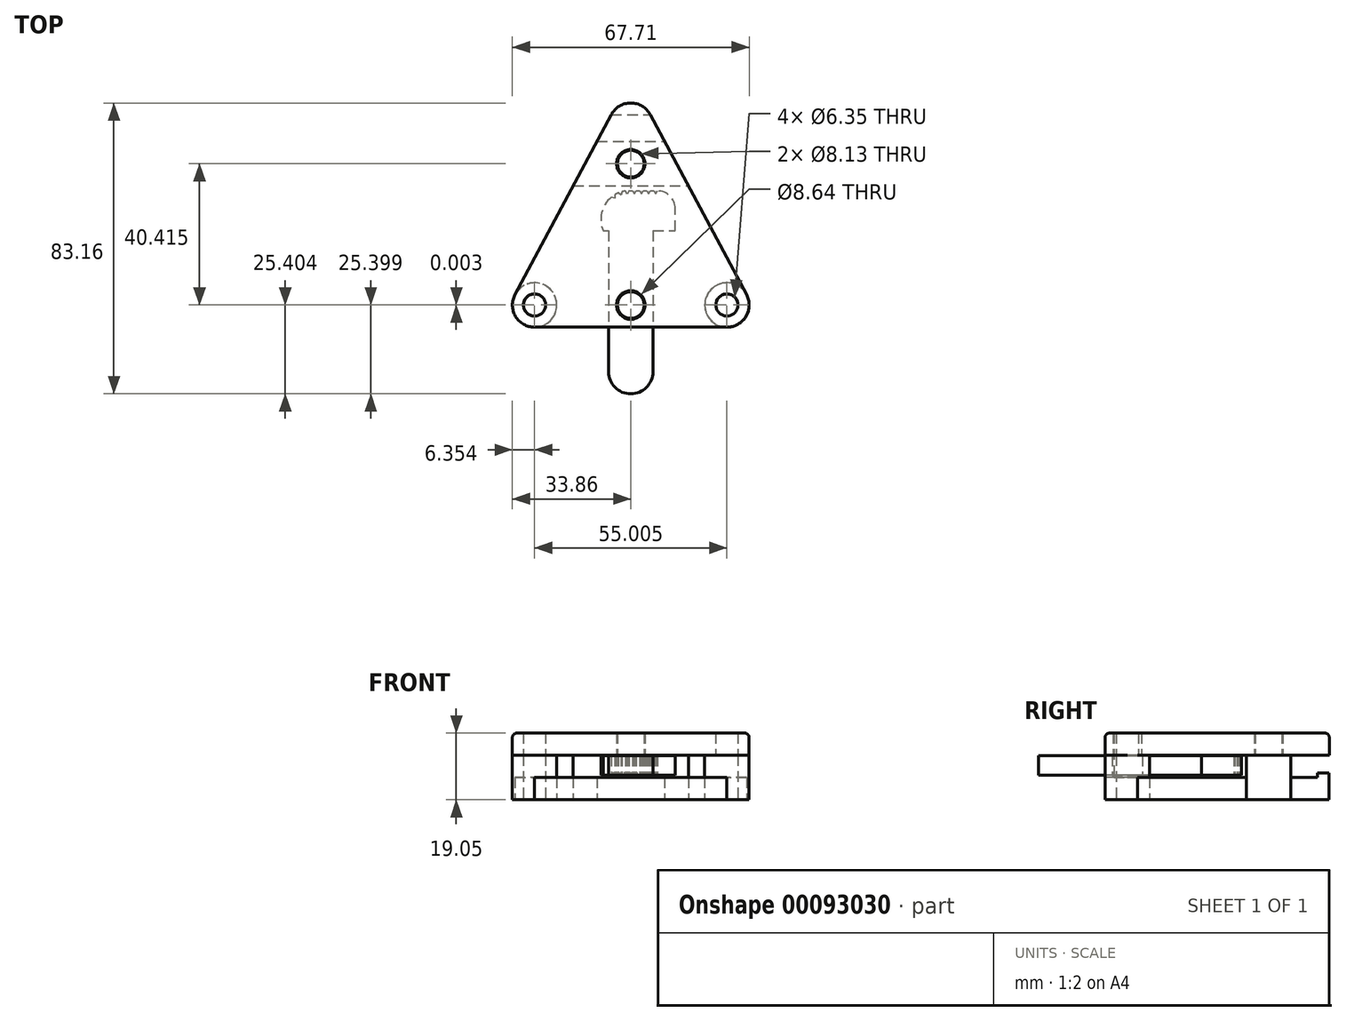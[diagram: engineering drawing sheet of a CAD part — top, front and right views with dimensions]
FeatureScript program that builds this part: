
annotation { "Feature Type Name" : "Feature", "Feature Type Description" : "" }
export const myFeature = defineFeature(function(context is Context, id is Id, definition is map)
    precondition{}
    {
        {
            var Q0;
            Q0=qCreatedBy(makeId("Top.planeOp"),FACE);
            var sketch = newSketch(context, id + "F0", { "sketchPlane" : qUnion([Q0])});
            skPoint(sketch, "E0.middle", {"position": v(0, 0) * mm});
            skLineSegment(sketch, "E1", {"start": v(27.5, -35.6) * mm, "end": v(-27.5, -35.6) * mm});
            skLineSegment(sketch, "E2", {"start": v(-33.1, -26.24) * mm, "end": v(-5.6, 25.13) * mm});
            skLineSegment(sketch, "E3", {"start": v(5.6, 25.13) * mm, "end": v(33.1, -26.24) * mm});
            skPoint(sketch, "E4.visualSharp", {"position": v(0, 35.6) * mm});
            skArc(sketch, "E4.filletArc", {"start": v(5.6, 25.13) * mm, "mid": v(0, 28.49) * mm, "end": v(-5.6, 25.13) * mm});
            skPoint(sketch, "E5.visualSharp", {"position": v(38.1, -35.6) * mm});
            skArc(sketch, "E5.filletArc", {"start": v(27.5, -35.6) * mm, "mid": v(32.95, -32.5) * mm, "end": v(33.1, -26.24) * mm});
            skPoint(sketch, "E6.visualSharp", {"position": v(-38.1, -35.6) * mm});
            skArc(sketch, "E6.filletArc", {"start": v(-33.1, -26.24) * mm, "mid": v(-32.95, -32.5) * mm, "end": v(-27.5, -35.6) * mm});
            skCircle(sketch, "E7", {"center": v(-27.5, -29.24) * mm, "radius": 3.18 * mm});
            skCircle(sketch, "E8", {"center": v(27.5, -29.24) * mm, "radius": 3.18 * mm});
            skPoint(sketch, "E9", {"position": v(0, -29.24) * mm});
            skCircle(sketch, "E10", {"center": v(0, -29.24) * mm, "radius": 3.81 * mm});
            skLineSegment(sketch, "E11", {"start": v(-5.6, 25.13) * mm, "end": v(5.6, 25.13) * mm});
            skLineSegment(sketch, "E12", {"start": v(-9.68, 17.51) * mm, "end": v(9.68, 17.51) * mm});
            skLineSegment(sketch, "E13", {"start": v(-16.47, 4.81) * mm, "end": v(16.47, 4.81) * mm});
            skCircle(sketch, "E14", {"center": v(-27.5, -29.24) * mm, "radius": 6.35 * mm});
            skCircle(sketch, "E15", {"center": v(27.5, -29.24) * mm, "radius": 6.35 * mm});
            skPoint(sketch, "E16", {"position": v(0, 11.16) * mm});
            skCircle(sketch, "E17", {"center": v(0, 11.16) * mm, "radius": 3.81 * mm});
            skSolve(sketch);
        }
        {
            var Q0;
            Q0=makeQuery(id+"F0.imprint","IMPRINT",FACE,{"disambiguationData":[TD([[makeQuery(id+"F0.imprint","IMPRINT",EDGE,{"derivedFrom":sQuery(id+"F0.wireOp",EDGE,"E1")}),-1.0]])]});
            var Q1;
            {var subQ0=sQuery(id+"F0.wireOp",EDGE,"E11");Q1=makeQuery(id+"F0.imprint","IMPRINT",FACE,{"disambiguationData":[TD([[makeQuery(id+"F0.imprint","IMPRINT",EDGE,{"derivedFrom":subQ0}),-1.0]])]});}
            extrude(context, id + "F1", {"entities" : qUnion([Q0, Q1]), "depth" : 6.35 * mm});
        }
        {
            var Q0;
            {var subQ0=sQuery(id+"F0.wireOp",EDGE,"E12");Q0=makeQuery(id+"F0.imprint","IMPRINT",FACE,{"disambiguationData":[TD([[makeQuery(id+"F0.imprint","IMPRINT",EDGE,{"derivedFrom":subQ0}),-1.0]])]});}
            var Q1;
            Q1=makeQuery(id+"F0.imprint","IMPRINT",FACE,{"disambiguationData":[TD([[makeQuery(id+"F0.imprint","IMPRINT",EDGE,{"derivedFrom":sQuery(id+"F0.wireOp",EDGE,"E7")}),-1.0]])]});
            var Q2;
            Q2=makeQuery(id+"F0.imprint","IMPRINT",FACE,{"disambiguationData":[TD([[makeQuery(id+"F0.imprint","IMPRINT",EDGE,{"derivedFrom":sQuery(id+"F0.wireOp",EDGE,"E8")}),-1.0]])]});
            extrude(context, id + "F2", {"entities" : qUnion([Q0, Q1, Q2]), "depth" : 12.7 * mm});
        }
        {
            var Q0;
            Q0=makeQuery(id+"F0.imprint","IMPRINT",FACE,{"disambiguationData":[TD([[makeQuery(id+"F0.imprint","IMPRINT",EDGE,{"derivedFrom":sQuery(id+"F0.wireOp",EDGE,"E10")}),1.0]])]});
            var Q1;
            Q1=makeQuery(id+"F0.imprint","IMPRINT",FACE,{"disambiguationData":[TD([[makeQuery(id+"F0.imprint","IMPRINT",EDGE,{"derivedFrom":sQuery(id+"F0.wireOp",EDGE,"E17")}),1.0]])]});
            extrude(context, id + "F3", {"entities" : qUnion([Q0, Q1]), "operationType" : NewBodyOperationType.ADD, "depth" : 19.05 * mm});
        }
        {
            var Q0;
            Q0=makeQuery(id+"F0.imprint","IMPRINT",FACE,{"disambiguationData":[TD([[makeQuery(id+"F0.imprint","IMPRINT",EDGE,{"derivedFrom":sQuery(id+"F0.wireOp",EDGE,"E4.filletArc")}),1.0]])]});
            extrude(context, id + "F4", {"entities" : qUnion([Q0]), "operationType" : NewBodyOperationType.ADD, "depth" : 7.62 * mm});
        }
        {
            var Q0;
            Q0=makeQuery(id+"F1.opExtrude","CAP_FACE",FACE,{"disambiguationData":[OSD([sQuery(id+"F0.wireOp",EDGE,"E1"),sQuery(id+"F0.wireOp",EDGE,"E2"),sQuery(id+"F0.wireOp",EDGE,"E3"),sQuery(id+"F0.wireOp",EDGE,"E10"),sQuery(id+"F0.wireOp",EDGE,"E13"),sQuery(id+"F0.wireOp",EDGE,"E14"),sQuery(id+"F0.wireOp",EDGE,"E15")])],"isStart":false});
            cPlane(context, id + "F5", {"entities" : qUnion([Q0]), "cplaneType" : CPlaneType.OFFSET, "offset" : 0 * mm, "width" : 152.4 * mm, "height" : 152.4 * mm});
        }
        {
            var Q0;
            Q0=qCreatedBy(id+"F5.planeOp",FACE);
            var sketch = newSketch(context, id + "F6", { "sketchPlane" : qUnion([Q0])});
            skLineSegment(sketch, "E18", {"start": v(-27.5, -35.59) * mm, "end": v(27.5, -35.59) * mm});
            skLineSegment(sketch, "E19", {"start": v(33.1, -26.24) * mm, "end": v(5.6, 25.17) * mm});
            skLineSegment(sketch, "E20", {"start": v(-5.6, 25.17) * mm, "end": v(-33.1, -26.24) * mm});
            skPoint(sketch, "E21.visualSharp", {"position": v(0, 35.64) * mm});
            skArc(sketch, "E21.filletArc", {"start": v(5.6, 25.17) * mm, "mid": v(0, 28.52) * mm, "end": v(-5.6, 25.17) * mm});
            skPoint(sketch, "E22.visualSharp", {"position": v(38.1, -35.59) * mm});
            skArc(sketch, "E22.filletArc", {"start": v(27.5, -35.59) * mm, "mid": v(32.95, -32.5) * mm, "end": v(33.1, -26.24) * mm});
            skPoint(sketch, "E23.visualSharp", {"position": v(-38.1, -35.59) * mm});
            skArc(sketch, "E23.filletArc", {"start": v(-33.1, -26.24) * mm, "mid": v(-32.95, -32.5) * mm, "end": v(-27.5, -35.59) * mm});
            skCircle(sketch, "E24", {"center": v(27.5, -29.24) * mm, "radius": 3.18 * mm});
            skCircle(sketch, "E25", {"center": v(-27.5, -29.24) * mm, "radius": 3.18 * mm});
            skCircle(sketch, "E26", {"center": v(0, -29.24) * mm, "radius": 4.06 * mm});
            skCircle(sketch, "E27", {"center": v(0, 11.18) * mm, "radius": 4.06 * mm});
            skSolve(sketch);
        }
        {
            var Q0;
            Q0=makeQuery(id+"F6.imprint","IMPRINT",FACE,{"disambiguationData":[TD([[makeQuery(id+"F6.imprint","IMPRINT",EDGE,{"derivedFrom":sQuery(id+"F6.wireOp",EDGE,"E18")}),1.0]])]});
            extrude(context, id + "F7", {"entities" : qUnion([Q0]), "depth" : 12.7 * mm, "hasSecondDirection" : true, "secondDirectionOppositeDirection" : false, "secondDirectionDepth" : 6.35 * mm});
        }
        {
            var Q0;
            Q0=makeQuery(id+"F7.opExtrude","CAP_EDGE",EDGE,{"disambiguationData":[OSD([sQuery(id+"F6.wireOp",EDGE,"E18")])],"isStart":false});
            fillet(context, id + "F8", {"entities" : qUnion([Q0]), "radius" : 1.27 * mm, "tangentPropagation" : true, "allowEdgeOverflow" : false});
        }
        {
            var Q0;
            Q0=qCreatedBy(id+"F5.planeOp",FACE);
            var sketch = newSketch(context, id + "F9", { "sketchPlane" : qUnion([Q0])});
            skLineSegment(sketch, "E28", {"start": v(-7.88, -8.03) * mm, "end": v(7.14, -8.03) * mm});
            skLineSegment(sketch, "E29.top", {"start": v(0, -54.64) * mm, "end": v(0, -54.64) * mm});
            skLineSegment(sketch, "E29.left", {"start": v(-6.35, -8.03) * mm, "end": v(-6.35, -48.3) * mm});
            skLineSegment(sketch, "E29.right", {"start": v(6.35, -8.03) * mm, "end": v(6.35, -48.3) * mm});
            skPoint(sketch, "E30", {"position": v(0, -54.64) * mm});
            skLineSegment(sketch, "E31", {"start": v(-0.5, 3.41) * mm, "end": v(-0.95, 2.5) * mm});
            skLineSegment(sketch, "E32", {"start": v(-0.95, 2.5) * mm, "end": v(-1.52, 3.34) * mm});
            skPoint(sketch, "E33", {"position": v(0, 3.41) * mm});
            skLineSegment(sketch, "E34", {"start": v(-2.54, 3.13) * mm, "end": v(-2.77, 2.14) * mm});
            skLineSegment(sketch, "E35", {"start": v(-2.77, 2.14) * mm, "end": v(-3.56, 2.78) * mm});
            skLineSegment(sketch, "E36", {"start": v(-4.57, 2.27) * mm, "end": v(-4.62, 1.25) * mm});
            skLineSegment(sketch, "E37", {"start": v(-4.62, 1.25) * mm, "end": v(-5.59, 1.55) * mm});
            skArc(sketch, "E38.trimOffspring", {"start": v(-1.52, 3.34) * mm, "mid": v(-2.04, 3.25) * mm, "end": v(-2.54, 3.13) * mm});
            skArc(sketch, "E39.trimOffspring", {"start": v(-3.56, 2.78) * mm, "mid": v(-4.07, 2.54) * mm, "end": v(-4.57, 2.27) * mm});
            skArc(sketch, "E40.trimOffspring", {"start": v(-5.59, 1.55) * mm, "mid": v(-8.34, -2.85) * mm, "end": v(-7.88, -8.03) * mm});
            skPoint(sketch, "E41.visualSharp", {"position": v(-6.35, -54.64) * mm});
            skArc(sketch, "E41.filletArc", {"start": v(-6.35, -48.3) * mm, "mid": v(-4.5, -52.78) * mm, "end": v(0, -54.64) * mm});
            skPoint(sketch, "E42.visualSharp", {"position": v(6.35, -54.64) * mm});
            skArc(sketch, "E42.filletArc", {"start": v(0, -54.64) * mm, "mid": v(4.5, -52.78) * mm, "end": v(6.35, -48.3) * mm});
            skCircle(sketch, "E43.0", {"center": v(0, -29.24) * mm, "radius": 4.32 * mm});
            skLineSegment(sketch, "E44", {"start": v(7.14, -8.03) * mm, "end": v(12.68, -8.03) * mm});
            skLineSegment(sketch, "E45", {"start": v(12.68, -8.03) * mm, "end": v(12.68, -1.67) * mm});
            skLineSegment(sketch, "E46", {"start": v(0, 3.41) * mm, "end": v(0.5, 3.41) * mm});
            skPoint(sketch, "E47.visualSharp", {"position": v(12.68, 3.41) * mm});
            skArc(sketch, "E47.filletArc", {"start": v(12.68, -1.67) * mm, "mid": v(11.19, 1.93) * mm, "end": v(7.6, 3.41) * mm});
            skLineSegment(sketch, "E48", {"start": v(-0.5, 3.41) * mm, "end": v(0, 3.41) * mm});
            skLineSegment(sketch, "E49", {"start": v(0.5, 3.41) * mm, "end": v(1.02, 2.53) * mm});
            skLineSegment(sketch, "E50", {"start": v(1.02, 2.53) * mm, "end": v(1.52, 3.41) * mm});
            skLineSegment(sketch, "E51", {"start": v(2.54, 3.41) * mm, "end": v(3.05, 2.53) * mm});
            skLineSegment(sketch, "E52", {"start": v(3.05, 2.53) * mm, "end": v(3.56, 3.41) * mm});
            skLineSegment(sketch, "E53", {"start": v(4.57, 3.41) * mm, "end": v(5.08, 2.53) * mm});
            skLineSegment(sketch, "E54", {"start": v(5.08, 2.53) * mm, "end": v(5.59, 3.41) * mm});
            skLineSegment(sketch, "E55", {"start": v(6.6, 3.41) * mm, "end": v(7.11, 2.53) * mm});
            skLineSegment(sketch, "E56", {"start": v(7.11, 2.53) * mm, "end": v(7.62, 3.41) * mm});
            skLineSegment(sketch, "E57.trimOffspring", {"start": v(5.59, 3.41) * mm, "end": v(6.6, 3.41) * mm});
            skLineSegment(sketch, "E58.trimOffspring", {"start": v(3.56, 3.41) * mm, "end": v(4.57, 3.41) * mm});
            skLineSegment(sketch, "E59.trimOffspring", {"start": v(1.52, 3.41) * mm, "end": v(2.54, 3.41) * mm});
            skSolve(sketch);
        }
        {
            var Q0;
            {var subQ1=sQuery(id+"F9.wireOp",EDGE,"E29.left");Q0=makeQuery(id+"F9.imprint","IMPRINT",FACE,{"disambiguationData":[TD([[makeQuery(id+"F9.imprint","IMPRINT",EDGE,{"derivedFrom":subQ1}),1.0]])]});}
            var Q1;
            {var subQ3=sQuery(id+"F9.wireOp",EDGE,"iZVFuVP9-M0Wl-WHxV-WEyo-qoywwQUfHX5c");Q1=makeQuery(id+"F9.imprint","IMPRINT",FACE,{"disambiguationData":[TD([[makeQuery(id+"F9.imprint","IMPRINT",EDGE,{"derivedFrom":subQ3}),1.0]])]});}
            var Q2;
            Q2=makeQuery(id+"F9.imprint","IMPRINT",FACE,{"disambiguationData":[TD([[makeQuery(id+"F9.imprint","IMPRINT",EDGE,{"derivedFrom":sQuery(id+"F9.wireOp",EDGE,"E31")}),1.0]])]});
            extrude(context, id + "F10", {"entities" : qUnion([Q0, Q1, Q2]), "depth" : 6.22 * mm, "hasSecondDirection" : true, "secondDirectionOppositeDirection" : false, "secondDirectionDepth" : 0.64 * mm});
        }
    });
